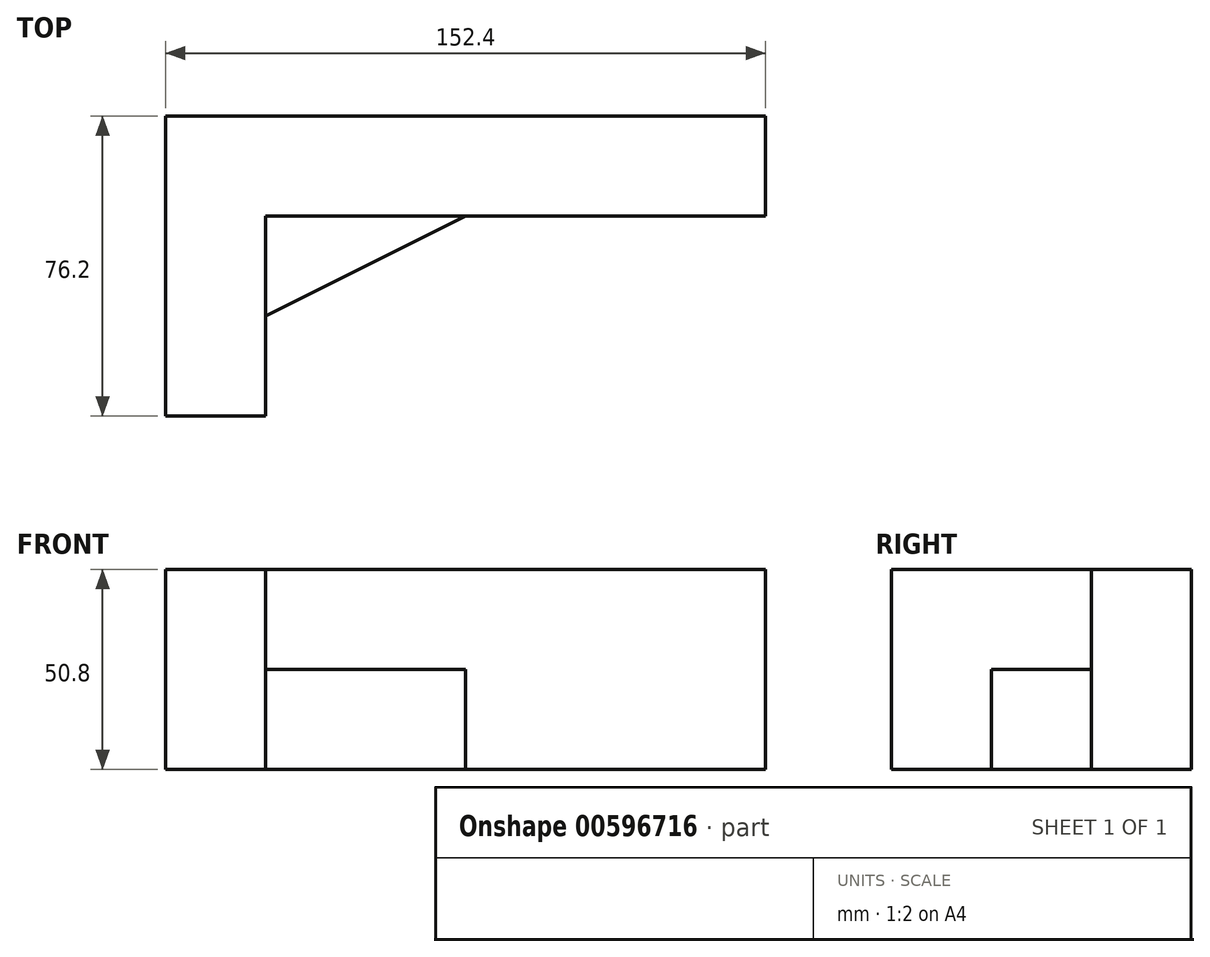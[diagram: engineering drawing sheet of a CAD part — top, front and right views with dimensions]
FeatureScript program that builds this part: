
annotation { "Feature Type Name" : "Feature", "Feature Type Description" : "" }
export const myFeature = defineFeature(function(context is Context, id is Id, definition is map)
    precondition{}
    {
        {
            var Q0;
            Q0=qCreatedBy(makeId("Front.planeOp"),FACE);
            var sketch = newSketch(context, id + "F0", { "sketchPlane" : qUnion([Q0])});
            skLineSegment(sketch, "E0.bottom", {"start": v(0, 0) * mm, "end": v(152.4, 0) * mm});
            skLineSegment(sketch, "E0.top", {"start": v(0, 50.8) * mm, "end": v(152.4, 50.8) * mm});
            skLineSegment(sketch, "E0.left", {"start": v(0, 0) * mm, "end": v(0, 50.8) * mm});
            skLineSegment(sketch, "E0.right", {"start": v(152.4, 0) * mm, "end": v(152.4, 50.8) * mm});
            skSolve(sketch);
        }
        {
            var Q0;
            Q0=makeQuery(id+"F0.imprint","IMPRINT",FACE,{"disambiguationData":[TD([[makeQuery(id+"F0.imprint","IMPRINT",EDGE,{"derivedFrom":sQuery(id+"F0.wireOp",EDGE,"E0.bottom")}),1.0]])]});
            extrude(context, id + "F1", {"entities" : qUnion([Q0]), "oppositeDirection" : true, "depth" : 25.4 * mm, "offsetDistance" : 25.4 * mm});
        }
        {
            var Q0;
            Q0=makeQuery(id+"F1.opExtrude","CAP_FACE",FACE,{"disambiguationData":[OSD([sQuery(id+"F0.wireOp",EDGE,"E0.bottom"),sQuery(id+"F0.wireOp",EDGE,"E0.top"),sQuery(id+"F0.wireOp",EDGE,"E0.left"),sQuery(id+"F0.wireOp",EDGE,"E0.right")])],"isStart":true});
            var sketch = newSketch(context, id + "F2", { "sketchPlane" : qUnion([Q0])});
            skLineSegment(sketch, "E1.bottom", {"start": v(0, 0) * mm, "end": v(25.4, 0) * mm});
            skLineSegment(sketch, "E1.top", {"start": v(0, 50.8) * mm, "end": v(25.4, 50.8) * mm});
            skLineSegment(sketch, "E1.left", {"start": v(0, 0) * mm, "end": v(0, 50.8) * mm});
            skLineSegment(sketch, "E1.right", {"start": v(25.4, 0) * mm, "end": v(25.4, 50.8) * mm});
            skSolve(sketch);
        }
        {
            var Q0;
            Q0=makeQuery(id+"F2.imprint","IMPRINT",FACE,{"disambiguationData":[TD([[makeQuery(id+"F2.imprint","IMPRINT",EDGE,{"derivedFrom":sQuery(id+"F2.wireOp",EDGE,"E1.bottom")}),1.0]])]});
            extrude(context, id + "F3", {"entities" : qUnion([Q0]), "operationType" : NewBodyOperationType.ADD, "depth" : 50.8 * mm, "offsetDistance" : 25.4 * mm});
        }
        {
            var Q0;
            Q0=makeQuery(id+"F1.opExtrude","CAP_FACE",FACE,{"disambiguationData":[OSD([sQuery(id+"F0.wireOp",EDGE,"E0.bottom"),sQuery(id+"F0.wireOp",EDGE,"E0.top"),sQuery(id+"F0.wireOp",EDGE,"E0.left"),sQuery(id+"F0.wireOp",EDGE,"E0.right")])],"isStart":true});
            var sketch = newSketch(context, id + "F4", { "sketchPlane" : qUnion([Q0])});
            skLineSegment(sketch, "E2.bottom", {"start": v(25.4, 0) * mm, "end": v(76.2, 0) * mm});
            skLineSegment(sketch, "E2.top", {"start": v(25.4, 25.4) * mm, "end": v(76.2, 25.4) * mm});
            skLineSegment(sketch, "E2.left", {"start": v(25.4, 0) * mm, "end": v(25.4, 25.4) * mm});
            skLineSegment(sketch, "E2.right", {"start": v(76.2, 0) * mm, "end": v(76.2, 25.4) * mm});
            skSolve(sketch);
        }
        {
            var Q0;
            Q0=makeQuery(id+"F4.imprint","IMPRINT",FACE,{"disambiguationData":[TD([[makeQuery(id+"F4.imprint","IMPRINT",EDGE,{"derivedFrom":sQuery(id+"F4.wireOp",EDGE,"E2.bottom")}),1.0]])]});
            extrude(context, id + "F5", {"entities" : qUnion([Q0]), "operationType" : NewBodyOperationType.ADD, "depth" : 25.4 * mm, "offsetDistance" : 25.4 * mm});
        }
        {
            var Q0;
            Q0=makeQuery(id+"F5.opExtrude","SWEPT_FACE",FACE,{"disambiguationData":[OSD([sQuery(id+"F4.wireOp",EDGE,"E2.top")])]});
            var sketch = newSketch(context, id + "F6", { "sketchPlane" : qUnion([Q0])});
            skLineSegment(sketch, "E3", {"start": v(25.4, 0) * mm, "end": v(25.4, -25.4) * mm});
            skLineSegment(sketch, "E4", {"start": v(25.4, -25.4) * mm, "end": v(76.2, 0) * mm});
            skLineSegment(sketch, "E5", {"start": v(76.2, 0) * mm, "end": v(25.4, 0) * mm});
            skSolve(sketch);
        }
        {
            var Q0;
            Q0=makeQuery(id+"F6.imprint","IMPRINT",FACE,{"disambiguationData":[TD([[makeQuery(id+"F6.imprint","IMPRINT",EDGE,{"derivedFrom":sQuery(id+"F6.wireOp",EDGE,"E4")}),-1.0]])]});
            extrude(context, id + "F7", {"entities" : qUnion([Q0]), "operationType" : NewBodyOperationType.REMOVE, "oppositeDirection" : true, "depth" : 25.4 * mm, "offsetDistance" : 25.4 * mm});
        }
    });
